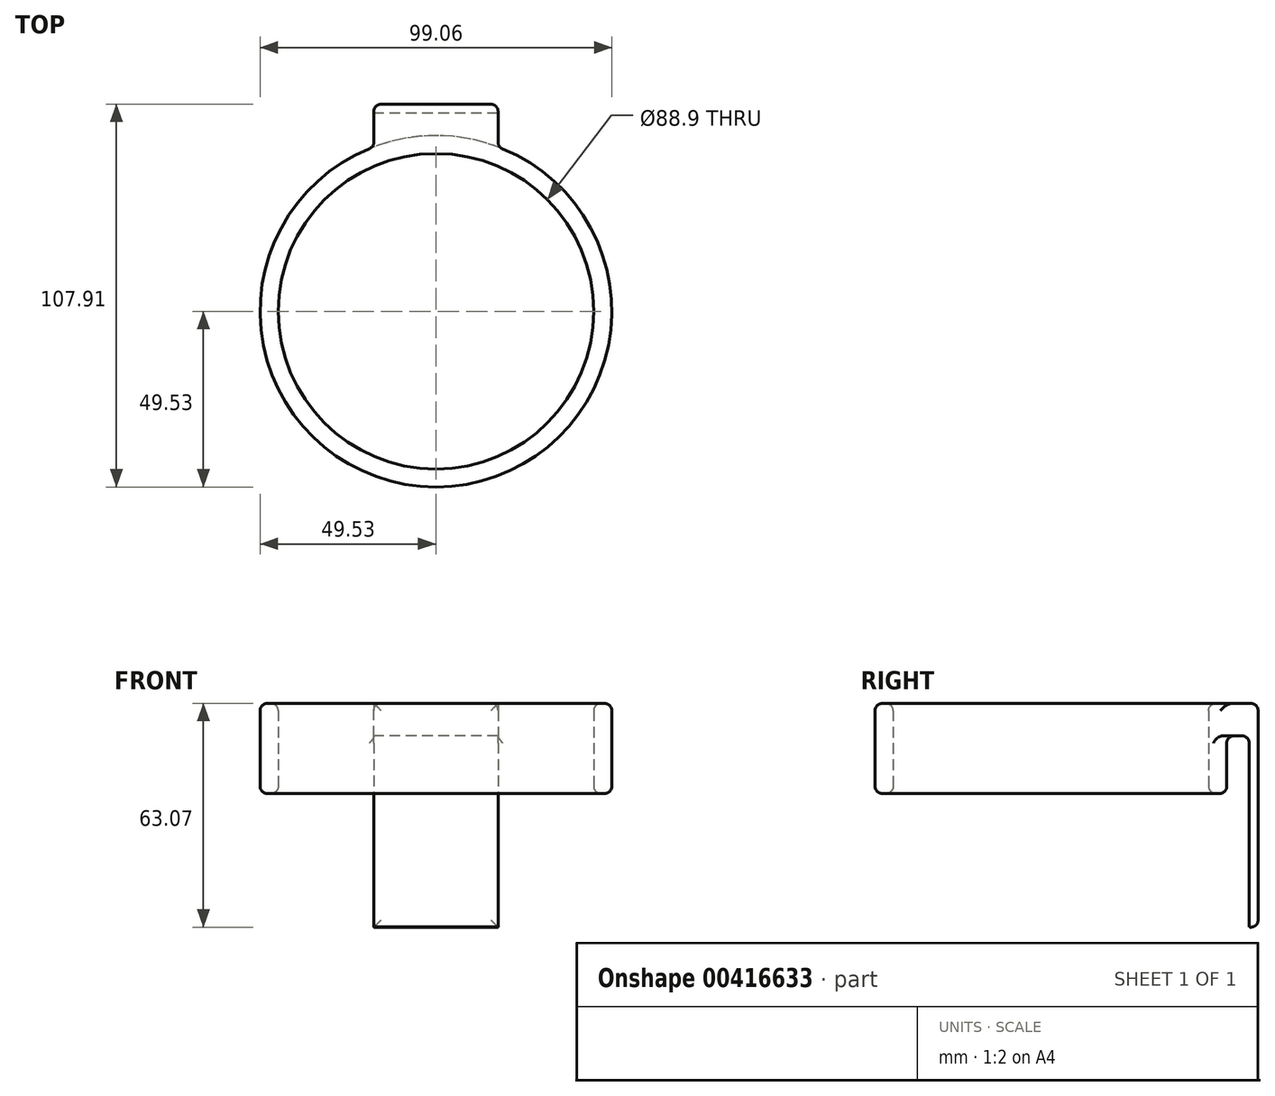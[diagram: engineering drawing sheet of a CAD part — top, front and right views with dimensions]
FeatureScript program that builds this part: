
annotation { "Feature Type Name" : "Feature", "Feature Type Description" : "" }
export const myFeature = defineFeature(function(context is Context, id is Id, definition is map)
    precondition{}
    {
        {
            var Q0;
            Q0=qCreatedBy(makeId("Top.planeOp"),FACE);
            var sketch = newSketch(context, id + "F0", { "sketchPlane" : qUnion([Q0])});
            skCircle(sketch, "E0", {"center": v(0, 0) * mm, "radius": 44.45 * mm});
            skCircle(sketch, "E1", {"center": v(0, 0) * mm, "radius": 49.53 * mm});
            skSolve(sketch);
        }
        {
            var Q0;
            Q0=qSketchRegion(id+"F0",true);
            extrude(context, id + "F1", {"entities" : qUnion([Q0]), "depth" : 25.4 * mm});
        }
        {
            var Q0;
            Q0=qCreatedBy(makeId("Right.planeOp"),FACE);
            var sketch = newSketch(context, id + "F2", { "sketchPlane" : qUnion([Q0])});
            skLineSegment(sketch, "E2", {"start": v(45.68, 25.4) * mm, "end": v(58.38, 25.4) * mm});
            skLineSegment(sketch, "E3", {"start": v(58.38, 25.4) * mm, "end": v(58.38, 25.4) * mm});
            skLineSegment(sketch, "E4", {"start": v(58.38, -38.1) * mm, "end": v(58.38, 25.4) * mm});
            skLineSegment(sketch, "E5", {"start": v(45.68, 25.4) * mm, "end": v(45.68, 16.24) * mm});
            skLineSegment(sketch, "E6", {"start": v(45.68, 16.24) * mm, "end": v(45.68, 16.24) * mm});
            skLineSegment(sketch, "E7", {"start": v(45.68, 16.24) * mm, "end": v(55.88, 16.24) * mm});
            skLineSegment(sketch, "E8", {"start": v(55.88, 16.24) * mm, "end": v(55.88, -37.61) * mm});
            skLineSegment(sketch, "E9", {"start": v(55.88, -37.61) * mm, "end": v(58.38, -38.1) * mm});
            skPoint(sketch, "E10.start.orphan", {"position": v(55.88, 17.2) * mm});
            skSolve(sketch);
        }
        {
            var Q0;
            Q0=qSketchRegion(id+"F2",true);
            var Q1;
            Q1=makeQuery(id+"F1.opExtrude","SWEPT_FACE",FACE,{"disambiguationData":[OSD([sQuery(id+"F0.wireOp",EDGE,"E1")])]});
            var Q2;
            Q2=makeQuery(id+"F1.opExtrude","SWEPT_BODY",BODY,{"disambiguationData":[OSD([sQuery(id+"F0.wireOp",EDGE,"E0"),sQuery(id+"F0.wireOp",EDGE,"E1")])]});
            extrude(context, id + "F3", {"entities" : qUnion([Q0]), "operationType" : NewBodyOperationType.ADD, "endBound" : BoundingType.SYMMETRIC, "endBoundEntityFace" : qUnion([Q1]), "endBoundEntityBody" : qUnion([Q2]), "depth" : 35 * mm});
        }
        {
            var Q0;
            Q0=makeQuery(id+"F3.opExtrude","SWEPT_EDGE",EDGE,{"disambiguationData":[OSD([sQuery(id+"F2.wireOp",EDGE,"E7"),sQuery(id+"F2.wireOp",EDGE,"E8")])]});
            var Q1;
            Q1=makeQuery(id+"F3.boolean.opBoolean","INTERSECT",EDGE,{"derivedFrom":[makeQuery(id+"F1.opExtrude","SWEPT_FACE",FACE,{"disambiguationData":[OSD([sQuery(id+"F0.wireOp",EDGE,"E1")])]}),makeQuery(id+"F3.opExtrude","SWEPT_FACE",FACE,{"disambiguationData":[OSD([sQuery(id+"F2.wireOp",EDGE,"E7")])]})]});
            var Q2;
            Q2=makeQuery(id+"F3.boolean.opBoolean","INTERSECT",EDGE,{"derivedFrom":[makeQuery(id+"F1.opExtrude","SWEPT_FACE",FACE,{"disambiguationData":[OSD([sQuery(id+"F0.wireOp",EDGE,"E1")])]}),makeQuery(id+"F3.opExtrude","CAP_FACE",FACE,{"disambiguationData":[OSD([sQuery(id+"F2.wireOp",EDGE,"E2"),sQuery(id+"F2.wireOp",EDGE,"E4"),sQuery(id+"F2.wireOp",EDGE,"E5"),sQuery(id+"F2.wireOp",EDGE,"E7"),sQuery(id+"F2.wireOp",EDGE,"E8"),sQuery(id+"F2.wireOp",EDGE,"E9")])],"isStart":false})]});
            var Q3;
            Q3=makeQuery(id+"F3.boolean.opBoolean","INTERSECT",EDGE,{"derivedFrom":[makeQuery(id+"F1.opExtrude","SWEPT_FACE",FACE,{"disambiguationData":[OSD([sQuery(id+"F0.wireOp",EDGE,"E1")])]}),makeQuery(id+"F3.opExtrude","CAP_FACE",FACE,{"disambiguationData":[OSD([sQuery(id+"F2.wireOp",EDGE,"E2"),sQuery(id+"F2.wireOp",EDGE,"E4"),sQuery(id+"F2.wireOp",EDGE,"E5"),sQuery(id+"F2.wireOp",EDGE,"E7"),sQuery(id+"F2.wireOp",EDGE,"E8"),sQuery(id+"F2.wireOp",EDGE,"E9")])],"isStart":true})]});
            var Q4;
            Q4=makeQuery(id+"F3.opExtrude","SWEPT_EDGE",EDGE,{"disambiguationData":[OSD([sQuery(id+"F2.wireOp",EDGE,"E2"),sQuery(id+"F2.wireOp",EDGE,"E4")])]});
            var Q5;
            Q5=makeQuery(id+"F1.opExtrude","CAP_EDGE",EDGE,{"disambiguationData":[OSD([sQuery(id+"F0.wireOp",EDGE,"E0")])],"isStart":false});
            var Q6;
            Q6=makeQuery(id+"F1.opExtrude","SWEPT_FACE",FACE,{"disambiguationData":[OSD([sQuery(id+"F0.wireOp",EDGE,"E1")])]});
            var Q7;
            Q7=makeQuery(id+"F1.opExtrude","SWEPT_FACE",FACE,{"disambiguationData":[OSD([sQuery(id+"F0.wireOp",EDGE,"E0")])]});
            var Q8;
            Q8=makeQuery(id+"F3.opExtrude","SWEPT_FACE",FACE,{"disambiguationData":[OSD([sQuery(id+"F2.wireOp",EDGE,"E4")])]});
            fillet(context, id + "F4", {"entities" : qUnion([Q0, Q1, Q2, Q3, Q4, Q5, Q6, Q7, Q8]), "radius" : 2 * mm, "tangentPropagation" : true, "allowEdgeOverflow" : false});
        }
    });
